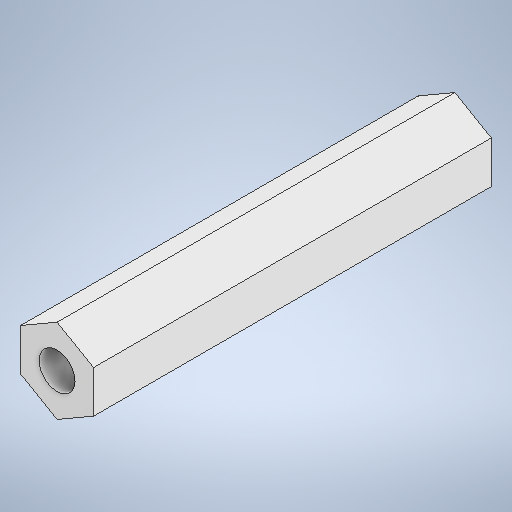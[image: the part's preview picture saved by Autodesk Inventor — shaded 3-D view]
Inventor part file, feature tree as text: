
AUTODESK INVENTOR PART (.ipt)
format: ipt  version: 2025.3 (Build 293356000, 356)  size: 225,792 bytes
history: native  units: mm
features: other x1, extrude x1
ambient origin geometry x8: Origin, YZ Plane, XZ Plane, XY Plane, X Axis, Y Axis, Z Axis, Center Point
bodies: Body1 (feature_tree)
feature tree (2):
  other  "ソリッド1"
  extrude  "押し出し1"  Depth=5.5mm
